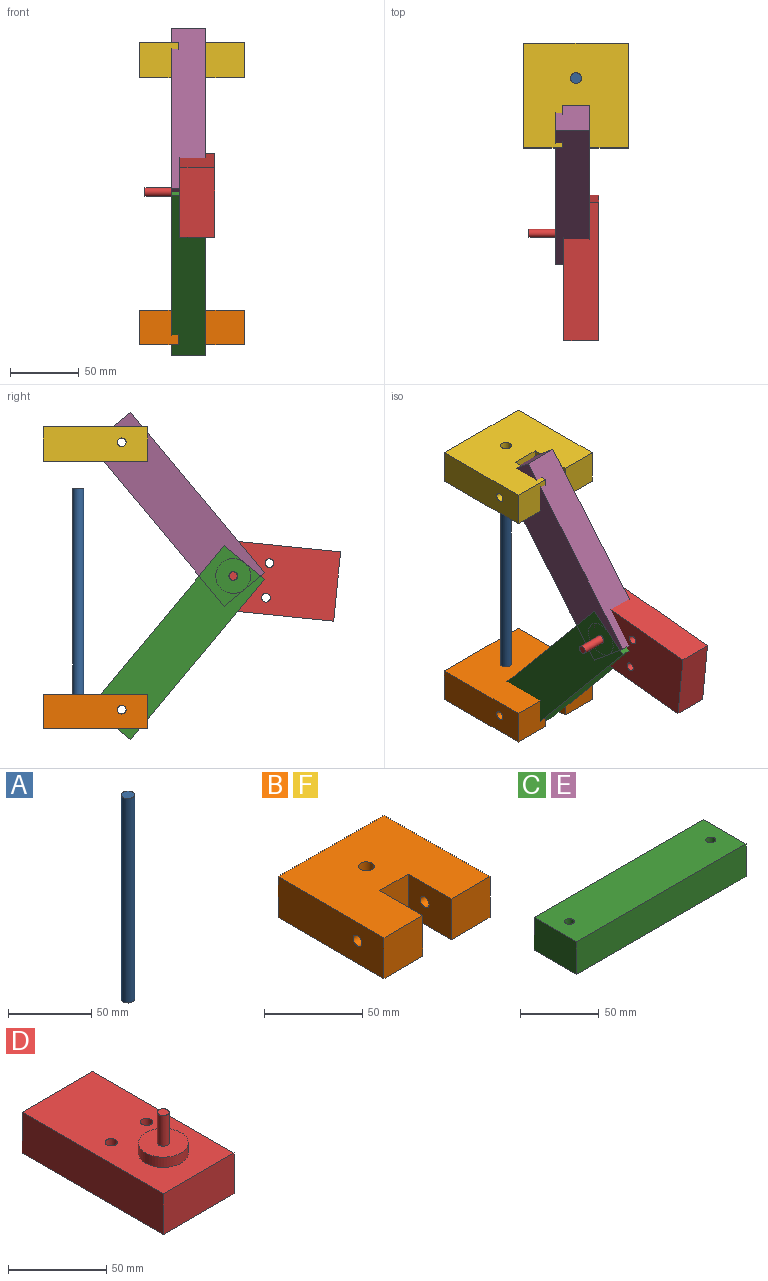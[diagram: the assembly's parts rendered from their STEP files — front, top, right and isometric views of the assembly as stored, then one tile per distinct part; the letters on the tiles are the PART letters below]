
ASSEMBLY  parts=6 mates=6
PART A: 3 faces, bbox 8x8x150 mm
  f0: cylinder r=4mm len=150mm, axis (0,0,-1), area 3769.9mm2, adj f1,f2
  f1: plane 8x8mm, normal (0,0,1), area 50.3mm2, adj f0
  f2: plane 8x8mm, normal (0,0,-1), area 50.3mm2, adj f0
PART B: 13 faces, bbox 76.2x76.2x25.4 mm
  f0: plane 76.2x25.4mm, normal (0,1,0), area 1935.5mm2, adj f1,f7,f8,f9
  f1: plane 76.2x25.4mm, normal (-1,0,0), area 1903.8mm2, adj f0,f2,f8,f9,f11
  f2: plane 27.94x25.4mm, normal (0,-1,0), area 709.7mm2, adj f1,f3,f8,f9
  f3: plane 30.94x25.4mm, normal (1,0,0), area 754.2mm2, adj f2,f4,f8,f9,f11
  f4: plane 25.4x20.32mm, normal (0,-1,0), area 516.1mm2, adj f3,f5,f8,f9
  f5: plane 30.94x25.4mm, normal (-1,0,0), area 754.2mm2, adj f4,f6,f8,f9,f10
  f6: plane 27.94x25.4mm, normal (0,-1,0), area 709.7mm2, adj f5,f7,f8,f9
  f7: plane 76.2x25.4mm, normal (1,0,0), area 1903.8mm2, adj f0,f6,f8,f9,f10
  f8: plane 76.2x76.2mm, normal (0,0,1), area 5127.5mm2, adj f0,f1,f2,f3,f4,f5,f6,f7
  f9: plane 76.2x76.2mm, normal (0,0,-1), area 5127.5mm2, adj f0,f1,f2,f3,f4,f5,f6,f7
  f10: cylinder r=3.17mm len=27.94mm, axis (-1,0,0), area 557.4mm2, adj f5,f7
  f11: cylinder r=3.17mm len=27.94mm, axis (-1,0,0), area 557.4mm2, adj f1,f3
  f12: cylinder r=4mm len=25.4mm, axis (0,0,-1), area 638.4mm2, adj f8,f9
PART C: 8 faces, bbox 152.4x38.1x25.4 mm
  f0: plane 38.1x25.4mm, normal (1,0,0), area 967.7mm2, adj f1,f3,f4,f5
  f1: plane 152.4x25.4mm, normal (0,1,0), area 3871mm2, adj f0,f2,f4,f5
  f2: plane 38.1x25.4mm, normal (-1,0,0), area 967.7mm2, adj f1,f3,f4,f5
  f3: plane 152.4x25.4mm, normal (0,-1,0), area 3871mm2, adj f0,f2,f4,f5
  f4: plane 152.4x38.1mm, normal (0,0,1), area 5743.1mm2, adj f0,f1,f2,f3,f6,f7
  f5: plane 152.4x38.1mm, normal (0,0,-1), area 5743.1mm2, adj f0,f1,f2,f3,f6,f7
  f6: cylinder r=3.17mm len=25.4mm, axis (0,0,-1), area 506.7mm2, adj f4,f5
  f7: cylinder r=3.17mm len=25.4mm, axis (0,0,-1), area 506.7mm2, adj f4,f5
PART D: 12 faces, bbox 50.8x101.6x50.8 mm
  f0: plane 50.8x25.4mm, normal (0,1,0), area 1290.3mm2, adj f1,f3,f4,f5
  f1: plane 101.6x25.4mm, normal (-1,0,0), area 2580.6mm2, adj f0,f2,f4,f5
  f2: plane 50.8x25.4mm, normal (0,-1,0), area 1290.3mm2, adj f1,f3,f4,f5
  f3: plane 101.6x25.4mm, normal (1,0,0), area 2580.6mm2, adj f0,f2,f4,f5
  f4: plane 101.6x50.8mm, normal (0,0,1), area 4591.2mm2, adj f0,f1,f2,f3,f6,f10,f11
  f5: plane 101.6x50.8mm, normal (0,0,-1), area 5097.9mm2, adj f0,f1,f2,f3,f10,f11
  f6: cylinder r=12.7mm len=25.4mm, axis (0,0,-1), area 506.7mm2, adj f4,f7
  f7: plane 25.4x25.4mm, normal (0,0,1), area 478.4mm2, adj f6,f8
  f8: cylinder r=3mm len=19.05mm, axis (0,0,-1), area 359.1mm2, adj f7,f9
  f9: plane 6x6mm, normal (0,0,1), area 28.3mm2, adj f8
  f10: cylinder r=3.17mm len=25.4mm, axis (0,0,-1), area 506.7mm2, adj f4,f5
  f11: cylinder r=3.17mm len=25.4mm, axis (0,0,-1), area 506.7mm2, adj f4,f5
PART E: same geometry as C
PART F: same geometry as B
PLACE A rot(axis=(0,0.9,-0.44),0deg) t=(159.27,-3.59,-64.22)mm
PLACE B rot(axis=(0,0.9,-0.44),0deg) t=(171.04,-26.65,-89.62)mm fixed
PLACE C rot(axis=(0.32,0.89,0.32),96.7deg) t=(144.03,-76.01,-26.83)mm
PLACE D rot(axis=(-0.71,-0.04,0.71),175.9deg) t=(175.78,-141.95,19.37)mm
PLACE E rot(axis=(-0.32,-0.89,0.32),96.7deg) t=(169.43,-76.01,70.7)mm
PLACE F t=(171.04,-26.65,105.43)mm
MATE revolute C.f6 <-> B.f10  axis (1,0,0) through (169.43,-35.34,-75.6)mm
MATE revolute E.f7 <-> D.f6  axis (-1,0,0) through (144.03,-116.68,21.93)mm
MATE revolute F.f10 <-> E.f6  axis (-1,0,0) through (169.43,-35.34,119.46)mm
MATE slider F.f12 <-> A.f0  axis (0,0,1) through (159.27,-3.59,130.83)mm
MATE revolute E.f7 <-> C.f7  axis (1,0,0) through (169.43,-116.68,21.93)mm
MATE fastened A.f0 <-> B.f12  axis (0,0,-1) through (159.27,-3.59,-64.22)mm
